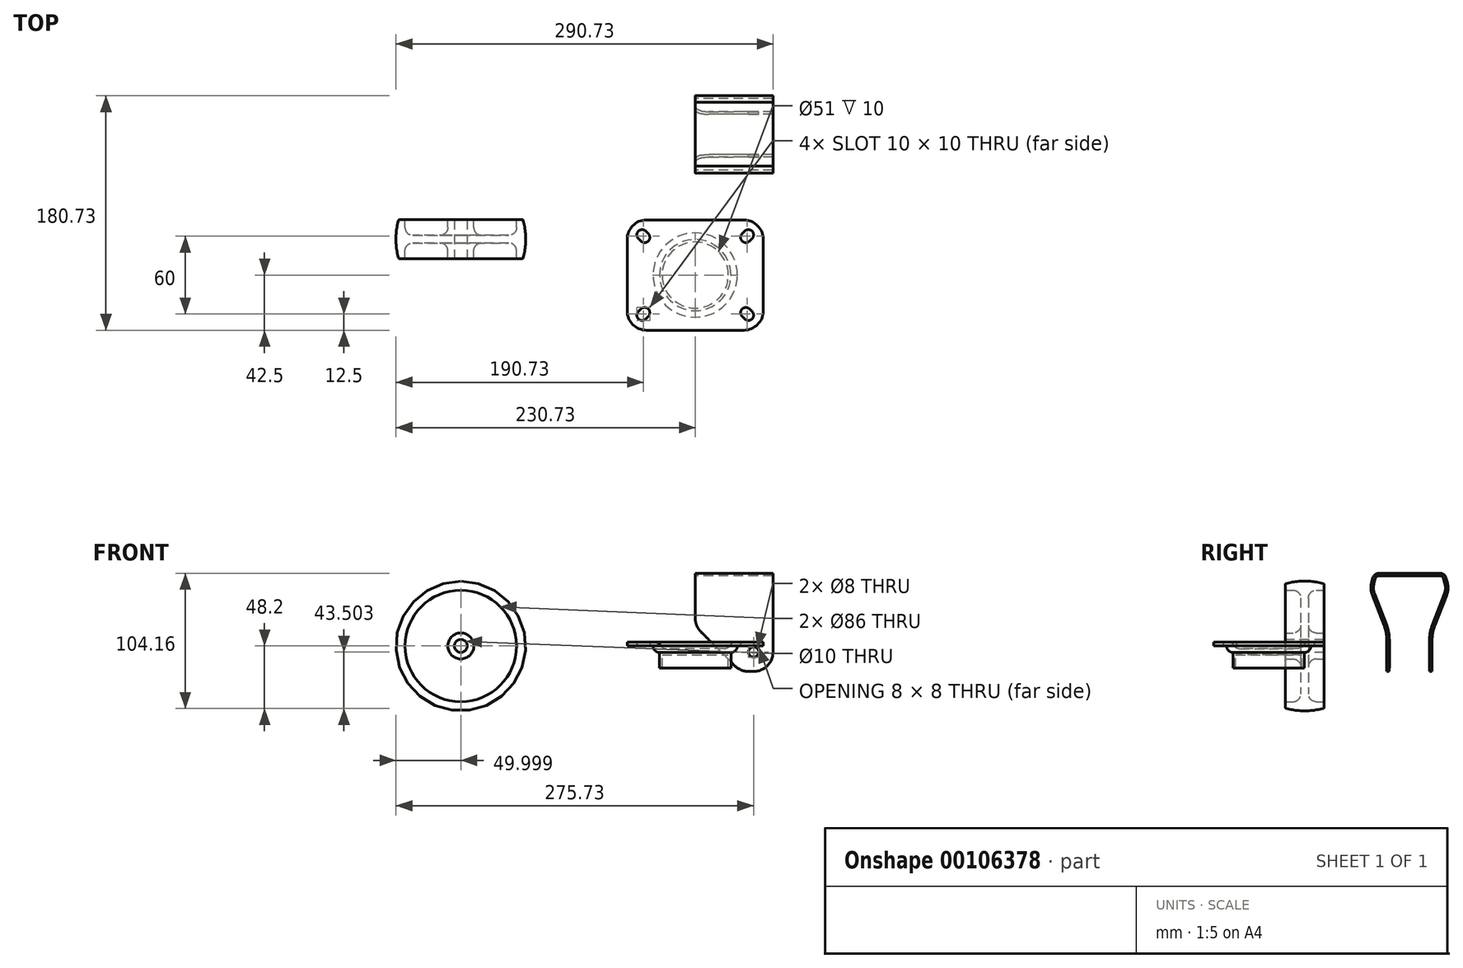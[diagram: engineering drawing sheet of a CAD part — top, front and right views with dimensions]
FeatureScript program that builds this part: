
annotation { "Feature Type Name" : "Feature", "Feature Type Description" : "" }
export const myFeature = defineFeature(function(context is Context, id is Id, definition is map)
    precondition{}
    {
        {
            var Q0;
            Q0=qCreatedBy(makeId("Top.planeOp"),FACE);
            var sketch = newSketch(context, id + "F0", { "sketchPlane" : qUnion([Q0])});
            skLineSegment(sketch, "E0.bottom", {"start": v(37.5, -42.5) * mm, "end": v(-37.5, -42.5) * mm});
            skLineSegment(sketch, "E0.top", {"start": v(37.5, 42.5) * mm, "end": v(-37.5, 42.5) * mm});
            skLineSegment(sketch, "E0.left", {"start": v(52.5, -27.5) * mm, "end": v(52.5, 27.5) * mm});
            skLineSegment(sketch, "E0.right", {"start": v(-52.5, -27.5) * mm, "end": v(-52.5, 27.5) * mm});
            skPoint(sketch, "E0.middle", {"position": v(0, 0) * mm});
            skLineSegment(sketch, "E1.bottom", {"start": v(41, -31) * mm, "end": v(-41, -31) * mm, "construction": true});
            skLineSegment(sketch, "E1.top", {"start": v(41, 31) * mm, "end": v(-41, 31) * mm, "construction": true});
            skLineSegment(sketch, "E1.left", {"start": v(41, -31) * mm, "end": v(41, 31) * mm, "construction": true});
            skLineSegment(sketch, "E1.right", {"start": v(-41, -31) * mm, "end": v(-41, 31) * mm, "construction": true});
            skLineSegment(sketch, "E2.bottom", {"start": v(39, -29) * mm, "end": v(-39, -29) * mm, "construction": true});
            skLineSegment(sketch, "E2.top", {"start": v(39, 29) * mm, "end": v(-39, 29) * mm, "construction": true});
            skLineSegment(sketch, "E2.left", {"start": v(39, -29) * mm, "end": v(39, 29) * mm, "construction": true});
            skLineSegment(sketch, "E2.right", {"start": v(-39, -29) * mm, "end": v(-39, 29) * mm, "construction": true});
            skArc(sketch, "E3", {"start": v(-38.17, 33.83) * mm, "mid": v(-43.83, 33.83) * mm, "end": v(-43.83, 28.17) * mm});
            skArc(sketch, "E4", {"start": v(-41.83, 26.17) * mm, "mid": v(-36.17, 26.17) * mm, "end": v(-36.17, 31.83) * mm});
            skLineSegment(sketch, "E5", {"start": v(-38.17, 33.83) * mm, "end": v(-36.17, 31.83) * mm});
            skLineSegment(sketch, "E6", {"start": v(-43.83, 28.17) * mm, "end": v(-41.83, 26.17) * mm});
            skLineSegment(sketch, "E7", {"start": v(0, 42.5) * mm, "end": v(0, -42.5) * mm, "construction": true});
            skLineSegment(sketch, "E8", {"start": v(-52.5, 0) * mm, "end": v(52.5, 0) * mm, "construction": true});
            skLineSegment(sketch, "E9.MirrorCS", {"start": v(43.83, 28.17) * mm, "end": v(41.83, 26.17) * mm});
            skLineSegment(sketch, "E10.MirrorCS", {"start": v(38.17, 33.83) * mm, "end": v(36.17, 31.83) * mm});
            skArc(sketch, "E11.MirrorCS", {"start": v(38.17, 33.83) * mm, "mid": v(43.83, 33.83) * mm, "end": v(43.83, 28.17) * mm});
            skArc(sketch, "E12.MirrorCS", {"start": v(41.83, 26.17) * mm, "mid": v(36.17, 26.17) * mm, "end": v(36.17, 31.83) * mm});
            skLineSegment(sketch, "E13.MirrorCS", {"start": v(52.5, 0) * mm, "end": v(-52.5, 0) * mm, "construction": true});
            skLineSegment(sketch, "E14.MirrorCS", {"start": v(43.83, -28.17) * mm, "end": v(41.83, -26.17) * mm});
            skLineSegment(sketch, "E15.MirrorCS", {"start": v(38.17, -33.83) * mm, "end": v(36.17, -31.83) * mm});
            skLineSegment(sketch, "E16.MirrorCS", {"start": v(-38.17, -33.83) * mm, "end": v(-36.17, -31.83) * mm});
            skLineSegment(sketch, "E17.MirrorCS", {"start": v(-43.83, -28.17) * mm, "end": v(-41.83, -26.17) * mm});
            skArc(sketch, "E18.MirrorCS", {"start": v(38.17, -33.83) * mm, "mid": v(43.83, -33.83) * mm, "end": v(43.83, -28.17) * mm});
            skArc(sketch, "E19.MirrorCS", {"start": v(41.83, -26.17) * mm, "mid": v(36.17, -26.17) * mm, "end": v(36.17, -31.83) * mm});
            skArc(sketch, "E20.MirrorCS", {"start": v(-38.17, -33.83) * mm, "mid": v(-43.83, -33.83) * mm, "end": v(-43.83, -28.17) * mm});
            skArc(sketch, "E21.MirrorCS", {"start": v(-41.83, -26.17) * mm, "mid": v(-36.17, -26.17) * mm, "end": v(-36.17, -31.83) * mm});
            skPoint(sketch, "E22.visualSharp", {"position": v(-52.5, 42.5) * mm});
            skArc(sketch, "E22.filletArc", {"start": v(-37.5, 42.5) * mm, "mid": v(-48.1, 38.1) * mm, "end": v(-52.5, 27.5) * mm});
            skPoint(sketch, "E23.visualSharp", {"position": v(-52.5, -42.5) * mm});
            skArc(sketch, "E23.filletArc", {"start": v(-52.5, -27.5) * mm, "mid": v(-48.1, -38.1) * mm, "end": v(-37.5, -42.5) * mm});
            skPoint(sketch, "E24.visualSharp", {"position": v(52.5, -42.5) * mm});
            skArc(sketch, "E24.filletArc", {"start": v(37.5, -42.5) * mm, "mid": v(48.1, -38.1) * mm, "end": v(52.5, -27.5) * mm});
            skPoint(sketch, "E25.visualSharp", {"position": v(52.5, 42.5) * mm});
            skArc(sketch, "E25.filletArc", {"start": v(52.5, 27.5) * mm, "mid": v(48.1, 38.1) * mm, "end": v(37.5, 42.5) * mm});
            skSolve(sketch);
        }
        {
            var Q0;
            Q0 = qSketchRegion(id + "F0", true);
            extrude(context, id + "F1", {"entities" : qUnion([Q0]), "depth" : 3 * mm});
        }
        {
            var Q0;
            Q0=makeQuery(id+"F1.opExtrude","CAP_FACE",FACE,{"disambiguationData":[OSD([sQuery(id+"F0.wireOp",EDGE,"E0.bottom"),sQuery(id+"F0.wireOp",EDGE,"E0.top"),sQuery(id+"F0.wireOp",EDGE,"E0.left"),sQuery(id+"F0.wireOp",EDGE,"E0.right"),sQuery(id+"F0.wireOp",EDGE,"E3"),sQuery(id+"F0.wireOp",EDGE,"E4"),sQuery(id+"F0.wireOp",EDGE,"E5"),sQuery(id+"F0.wireOp",EDGE,"E6"),sQuery(id+"F0.wireOp",EDGE,"E9.MirrorCS"),sQuery(id+"F0.wireOp",EDGE,"E10.MirrorCS"),sQuery(id+"F0.wireOp",EDGE,"E11.MirrorCS"),sQuery(id+"F0.wireOp",EDGE,"E12.MirrorCS"),sQuery(id+"F0.wireOp",EDGE,"E14.MirrorCS"),sQuery(id+"F0.wireOp",EDGE,"E15.MirrorCS"),sQuery(id+"F0.wireOp",EDGE,"E16.MirrorCS"),sQuery(id+"F0.wireOp",EDGE,"E17.MirrorCS"),sQuery(id+"F0.wireOp",EDGE,"E18.MirrorCS"),sQuery(id+"F0.wireOp",EDGE,"E20.MirrorCS"),sQuery(id+"F0.wireOp",EDGE,"E21.MirrorCS"),sQuery(id+"F0.wireOp",EDGE,"E19.MirrorCS"),sQuery(id+"F0.wireOp",EDGE,"E22.filletArc"),sQuery(id+"F0.wireOp",EDGE,"E23.filletArc"),sQuery(id+"F0.wireOp",EDGE,"E24.filletArc"),sQuery(id+"F0.wireOp",EDGE,"E25.filletArc")])],"isStart":true});
            var sketch = newSketch(context, id + "F2", { "sketchPlane" : qUnion([Q0])});
            skCircle(sketch, "E26", {"center": v(0, 0) * mm, "radius": 32.5 * mm});
            skSolve(sketch);
        }
        {
            var Q0;
            Q0 = qSketchRegion(id + "F2", true);
            extrude(context, id + "F3", {"entities" : qUnion([Q0]), "operationType" : NewBodyOperationType.ADD, "depth" : 5 * mm});
        }
        {
            var Q0;
            Q0=makeQuery(id+"F3.opExtrude","CAP_EDGE",EDGE,{"disambiguationData":[OSD([sQuery(id+"F2.wireOp",EDGE,"E26")])],"isStart":false});
            fillet(context, id + "F4", {"entities" : qUnion([Q0]), "radius" : 5 * mm, "tangentPropagation" : true, "allowEdgeOverflow" : false});
        }
        {
            var Q0;
            Q0=makeQuery(id+"F1.opExtrude","CAP_FACE",FACE,{"disambiguationData":[OSD([sQuery(id+"F0.wireOp",EDGE,"E0.bottom"),sQuery(id+"F0.wireOp",EDGE,"E0.top"),sQuery(id+"F0.wireOp",EDGE,"E0.left"),sQuery(id+"F0.wireOp",EDGE,"E0.right"),sQuery(id+"F0.wireOp",EDGE,"E3"),sQuery(id+"F0.wireOp",EDGE,"E4"),sQuery(id+"F0.wireOp",EDGE,"E5"),sQuery(id+"F0.wireOp",EDGE,"E6"),sQuery(id+"F0.wireOp",EDGE,"E9.MirrorCS"),sQuery(id+"F0.wireOp",EDGE,"E10.MirrorCS"),sQuery(id+"F0.wireOp",EDGE,"E11.MirrorCS"),sQuery(id+"F0.wireOp",EDGE,"E12.MirrorCS"),sQuery(id+"F0.wireOp",EDGE,"E14.MirrorCS"),sQuery(id+"F0.wireOp",EDGE,"E15.MirrorCS"),sQuery(id+"F0.wireOp",EDGE,"E16.MirrorCS"),sQuery(id+"F0.wireOp",EDGE,"E17.MirrorCS"),sQuery(id+"F0.wireOp",EDGE,"E18.MirrorCS"),sQuery(id+"F0.wireOp",EDGE,"E20.MirrorCS"),sQuery(id+"F0.wireOp",EDGE,"E21.MirrorCS"),sQuery(id+"F0.wireOp",EDGE,"E19.MirrorCS"),sQuery(id+"F0.wireOp",EDGE,"E22.filletArc"),sQuery(id+"F0.wireOp",EDGE,"E23.filletArc"),sQuery(id+"F0.wireOp",EDGE,"E24.filletArc"),sQuery(id+"F0.wireOp",EDGE,"E25.filletArc")])],"isStart":false});
            var sketch = newSketch(context, id + "F5", { "sketchPlane" : qUnion([Q0])});
            skCircle(sketch, "E27", {"center": v(0, 0) * mm, "radius": 27.5 * mm});
            skSolve(sketch);
        }
        {
            var Q0;
            Q0 = qSketchRegion(id + "F5", true);
            extrude(context, id + "F6", {"entities" : qUnion([Q0]), "operationType" : NewBodyOperationType.REMOVE, "oppositeDirection" : true, "depth" : 5 * mm});
        }
        {
            var Q0;
            Q0=makeQuery(id+"F6.boolean.opBoolean","COPY",EDGE,{"derivedFrom":makeQuery(id+"F6.opExtrude","CAP_EDGE",EDGE,{"disambiguationData":[OSD([sQuery(id+"F5.wireOp",EDGE,"E27")])],"isStart":false})});
            fillet(context, id + "F7", {"entities" : qUnion([Q0]), "radius" : 5 * mm, "tangentPropagation" : true, "allowEdgeOverflow" : false});
        }
        {
            var Q0;
            Q0=makeQuery(id+"F7.opFillet","BLEND_EDGE",EDGE,{"blendedFrom":[makeQuery(id+"F6.boolean.opBoolean","COPY",EDGE,{"derivedFrom":makeQuery(id+"F6.opExtrude","CAP_EDGE",EDGE,{"disambiguationData":[OSD([sQuery(id+"F5.wireOp",EDGE,"E27")])],"isStart":false})}),makeQuery(id+"F1.opExtrude","CAP_FACE",FACE,{"disambiguationData":[OSD([sQuery(id+"F0.wireOp",EDGE,"E0.bottom"),sQuery(id+"F0.wireOp",EDGE,"E0.top"),sQuery(id+"F0.wireOp",EDGE,"E0.left"),sQuery(id+"F0.wireOp",EDGE,"E0.right"),sQuery(id+"F0.wireOp",EDGE,"E3"),sQuery(id+"F0.wireOp",EDGE,"E4"),sQuery(id+"F0.wireOp",EDGE,"E5"),sQuery(id+"F0.wireOp",EDGE,"E6"),sQuery(id+"F0.wireOp",EDGE,"E9.MirrorCS"),sQuery(id+"F0.wireOp",EDGE,"E10.MirrorCS"),sQuery(id+"F0.wireOp",EDGE,"E11.MirrorCS"),sQuery(id+"F0.wireOp",EDGE,"E12.MirrorCS"),sQuery(id+"F0.wireOp",EDGE,"E14.MirrorCS"),sQuery(id+"F0.wireOp",EDGE,"E15.MirrorCS"),sQuery(id+"F0.wireOp",EDGE,"E16.MirrorCS"),sQuery(id+"F0.wireOp",EDGE,"E17.MirrorCS"),sQuery(id+"F0.wireOp",EDGE,"E18.MirrorCS"),sQuery(id+"F0.wireOp",EDGE,"E20.MirrorCS"),sQuery(id+"F0.wireOp",EDGE,"E21.MirrorCS"),sQuery(id+"F0.wireOp",EDGE,"E19.MirrorCS"),sQuery(id+"F0.wireOp",EDGE,"E22.filletArc"),sQuery(id+"F0.wireOp",EDGE,"E23.filletArc"),sQuery(id+"F0.wireOp",EDGE,"E24.filletArc"),sQuery(id+"F0.wireOp",EDGE,"E25.filletArc")])],"isStart":false})],"blendedInto":[makeQuery(id+"F1.opExtrude","CAP_FACE",FACE,{"disambiguationData":[OSD([sQuery(id+"F0.wireOp",EDGE,"E0.bottom"),sQuery(id+"F0.wireOp",EDGE,"E0.top"),sQuery(id+"F0.wireOp",EDGE,"E0.left"),sQuery(id+"F0.wireOp",EDGE,"E0.right"),sQuery(id+"F0.wireOp",EDGE,"E3"),sQuery(id+"F0.wireOp",EDGE,"E4"),sQuery(id+"F0.wireOp",EDGE,"E5"),sQuery(id+"F0.wireOp",EDGE,"E6"),sQuery(id+"F0.wireOp",EDGE,"E9.MirrorCS"),sQuery(id+"F0.wireOp",EDGE,"E10.MirrorCS"),sQuery(id+"F0.wireOp",EDGE,"E11.MirrorCS"),sQuery(id+"F0.wireOp",EDGE,"E12.MirrorCS"),sQuery(id+"F0.wireOp",EDGE,"E14.MirrorCS"),sQuery(id+"F0.wireOp",EDGE,"E15.MirrorCS"),sQuery(id+"F0.wireOp",EDGE,"E16.MirrorCS"),sQuery(id+"F0.wireOp",EDGE,"E17.MirrorCS"),sQuery(id+"F0.wireOp",EDGE,"E18.MirrorCS"),sQuery(id+"F0.wireOp",EDGE,"E20.MirrorCS"),sQuery(id+"F0.wireOp",EDGE,"E21.MirrorCS"),sQuery(id+"F0.wireOp",EDGE,"E19.MirrorCS"),sQuery(id+"F0.wireOp",EDGE,"E22.filletArc"),sQuery(id+"F0.wireOp",EDGE,"E23.filletArc"),sQuery(id+"F0.wireOp",EDGE,"E24.filletArc"),sQuery(id+"F0.wireOp",EDGE,"E25.filletArc")])],"isStart":false})]});
            fillet(context, id + "F8", {"entities" : qUnion([Q0]), "radius" : 5 * mm, "tangentPropagation" : true, "allowEdgeOverflow" : false});
        }
        {
            var Q0;
            Q0=makeQuery(id+"F3.opExtrude","CAP_FACE",FACE,{"disambiguationData":[OSD([sQuery(id+"F2.wireOp",EDGE,"E26")])],"isStart":false});
            var sketch = newSketch(context, id + "F9", { "sketchPlane" : qUnion([Q0])});
            skCircle(sketch, "E28", {"center": v(0, 0) * mm, "radius": 27.5 * mm});
            skSolve(sketch);
        }
        {
            var Q0;
            Q0 = qSketchRegion(id + "F9", true);
            extrude(context, id + "F10", {"entities" : qUnion([Q0]), "depth" : 2 * mm});
        }
        {
            var Q0;
            Q0=makeQuery(id+"F10.opExtrude","CAP_FACE",FACE,{"disambiguationData":[OSD([sQuery(id+"F9.wireOp",EDGE,"E28")])],"isStart":false});
            var sketch = newSketch(context, id + "F11", { "sketchPlane" : qUnion([Q0])});
            skCircle(sketch, "E29", {"center": v(0, 0) * mm, "radius": 27.5 * mm});
            skCircle(sketch, "E30.0", {"center": v(0, 0) * mm, "radius": 25.5 * mm});
            skSolve(sketch);
        }
        {
            var Q0;
            Q0 = qSketchRegion(id + "F11", true);
            extrude(context, id + "F12", {"entities" : qUnion([Q0]), "operationType" : NewBodyOperationType.ADD, "depth" : 10 * mm});
        }
        {
            var Q0;
            Q0=qCreatedBy(makeId("Top.planeOp"),FACE);
            var sketch = newSketch(context, id + "F13", { "sketchPlane" : qUnion([Q0])});
            skLineSegment(sketch, "E31.bottom", {"start": v(-230.73, 12.69) * mm, "end": v(-130.73, 12.69) * mm, "construction": true});
            skLineSegment(sketch, "E31.top", {"start": v(-230.73, 42.69) * mm, "end": v(-130.73, 42.69) * mm, "construction": true});
            skLineSegment(sketch, "E31.right", {"start": v(-130.73, 12.69) * mm, "end": v(-130.73, 42.69) * mm, "construction": true});
            skLineSegment(sketch, "E32", {"start": v(-130.73, 27.69) * mm, "end": v(-230.73, 27.69) * mm, "construction": true});
            skLineSegment(sketch, "E33", {"start": v(-230.73, 42.69) * mm, "end": v(-230.73, 12.69) * mm, "construction": true});
            skLineSegment(sketch, "E34", {"start": v(-180.73, 42.69) * mm, "end": v(-180.73, 12.69) * mm, "construction": true});
            skLineSegment(sketch, "E35", {"start": v(-180.73, 27.69) * mm, "end": v(-180.73, 42.69) * mm});
            skLineSegment(sketch, "E36", {"start": v(-190.73, 41.69) * mm, "end": v(-190.73, 36.69) * mm});
            skLineSegment(sketch, "E37", {"start": v(-196.73, 30.69) * mm, "end": v(-217.73, 30.69) * mm});
            skLineSegment(sketch, "E38", {"start": v(-223.73, 36.69) * mm, "end": v(-223.73, 41.69) * mm});
            skLineSegment(sketch, "E39", {"start": v(-224.73, 42.69) * mm, "end": v(-227.96, 42.69) * mm});
            skPoint(sketch, "E40.visualSharp", {"position": v(-223.73, 30.69) * mm});
            skArc(sketch, "E40.filletArc", {"start": v(-223.73, 36.69) * mm, "mid": v(-221.97, 32.45) * mm, "end": v(-217.73, 30.69) * mm});
            skPoint(sketch, "E41.visualSharp", {"position": v(-190.73, 30.69) * mm});
            skArc(sketch, "E41.filletArc", {"start": v(-196.73, 30.69) * mm, "mid": v(-192.49, 32.45) * mm, "end": v(-190.73, 36.69) * mm});
            skArc(sketch, "E42", {"start": v(-228.93, 41.94) * mm, "mid": v(-230.73, 27.69) * mm, "end": v(-228.93, 13.44) * mm});
            skLineSegment(sketch, "E43", {"start": v(-189.73, 42.69) * mm, "end": v(-180.73, 42.69) * mm});
            skArc(sketch, "E44.MirrorCS", {"start": v(-223.73, 18.69) * mm, "mid": v(-221.97, 22.93) * mm, "end": v(-217.73, 24.69) * mm});
            skLineSegment(sketch, "E45.MirrorCS", {"start": v(-196.73, 24.69) * mm, "end": v(-217.73, 24.69) * mm});
            skLineSegment(sketch, "E46.MirrorCS", {"start": v(-223.73, 18.69) * mm, "end": v(-223.73, 13.69) * mm});
            skLineSegment(sketch, "E47.MirrorCS", {"start": v(-224.73, 12.69) * mm, "end": v(-227.96, 12.69) * mm});
            skArc(sketch, "E48.MirrorCS", {"start": v(-196.73, 24.69) * mm, "mid": v(-192.49, 22.93) * mm, "end": v(-190.73, 18.69) * mm});
            skLineSegment(sketch, "E49.MirrorCS", {"start": v(-190.73, 13.69) * mm, "end": v(-190.73, 18.69) * mm});
            skLineSegment(sketch, "E50.MirrorCS", {"start": v(-189.73, 12.69) * mm, "end": v(-180.73, 12.69) * mm});
            skLineSegment(sketch, "E51.MirrorCS", {"start": v(-180.73, 27.69) * mm, "end": v(-180.73, 12.69) * mm});
            skPoint(sketch, "E52.visualSharp", {"position": v(-228.73, 42.69) * mm});
            skArc(sketch, "E52.filletArc", {"start": v(-227.96, 42.69) * mm, "mid": v(-228.57, 42.48) * mm, "end": v(-228.93, 41.94) * mm});
            skPoint(sketch, "E53.visualSharp", {"position": v(-223.73, 42.69) * mm});
            skArc(sketch, "E53.filletArc", {"start": v(-223.73, 41.69) * mm, "mid": v(-224.02, 42.4) * mm, "end": v(-224.73, 42.69) * mm});
            skPoint(sketch, "E54.visualSharp", {"position": v(-190.73, 42.69) * mm});
            skArc(sketch, "E54.filletArc", {"start": v(-189.73, 42.69) * mm, "mid": v(-190.44, 42.4) * mm, "end": v(-190.73, 41.69) * mm});
            skPoint(sketch, "E55.visualSharp", {"position": v(-228.73, 12.69) * mm});
            skArc(sketch, "E55.filletArc", {"start": v(-228.93, 13.44) * mm, "mid": v(-228.57, 12.9) * mm, "end": v(-227.96, 12.69) * mm});
            skPoint(sketch, "E56.visualSharp", {"position": v(-223.73, 12.69) * mm});
            skArc(sketch, "E56.filletArc", {"start": v(-224.73, 12.69) * mm, "mid": v(-224.02, 12.98) * mm, "end": v(-223.73, 13.69) * mm});
            skPoint(sketch, "E57.visualSharp", {"position": v(-190.73, 12.69) * mm});
            skArc(sketch, "E57.filletArc", {"start": v(-190.73, 13.69) * mm, "mid": v(-190.44, 12.98) * mm, "end": v(-189.73, 12.69) * mm});
            skSolve(sketch);
        }
        {
            var Q0;
            Q0=sQuery(id+"F13.wireOp",VERTEX,"E51.MirrorCS.start");
            var Q1;
            Q1=qCreatedBy(makeId("Front.planeOp"),FACE);
            cPlane(context, id + "F14", {"entities" : qUnion([Q0, Q1]), "cplaneType" : CPlaneType.PLANE_POINT, "offset" : 25 * mm, "width" : 150 * mm, "height" : 150 * mm});
        }
        {
            var Q0;
            Q0=makeQuery(id+"F13.imprint","IMPRINT",FACE,{"disambiguationData":[TD([[makeQuery(id+"F13.imprint","IMPRINT",EDGE,{"derivedFrom":sQuery(id+"F13.wireOp",EDGE,"E35")}),1.0]])]});
            var Q1;
            Q1=sQuery(id+"F13.wireOp",EDGE,"E51.MirrorCS");
            revolve(context, id + "F15", {"entities" : qUnion([Q0]), "axis" : qUnion([Q1]), "revolveType" : RevolveType.FULL});
        }
        {
            var Q0;
            Q0=makeQuery(id+"F15.opRevolve","SWEPT_FACE",FACE,{"disambiguationData":[OSD([sQuery(id+"F13.wireOp",EDGE,"E50.MirrorCS")])]});
            var sketch = newSketch(context, id + "F16", { "sketchPlane" : qUnion([Q0])});
            skCircle(sketch, "E58", {"center": v(-180.73, 0) * mm, "radius": 5 * mm});
            skSolve(sketch);
        }
        {
            var Q0;
            Q0 = qSketchRegion(id + "F16", true);
            extrude(context, id + "F17", {"entities" : qUnion([Q0]), "operationType" : NewBodyOperationType.REMOVE, "endBound" : BoundingType.THROUGH_ALL, "oppositeDirection" : true, "depth" : 25 * mm});
        }
        {
            var Q0;
            Q0=qCreatedBy(makeId("Right.planeOp"),FACE);
            var sketch = newSketch(context, id + "F18", { "sketchPlane" : qUnion([Q0])});
            skLineSegment(sketch, "E59.bottom", {"start": v(135.97, -19.7) * mm, "end": v(80.97, -19.7) * mm, "construction": true});
            skLineSegment(sketch, "E59.left", {"start": v(135.97, -19.7) * mm, "end": v(136, 55.3) * mm, "construction": true});
            skLineSegment(sketch, "E59.right", {"start": v(80.97, -19.7) * mm, "end": v(81, 55.3) * mm, "construction": true});
            skPoint(sketch, "E59.middle", {"position": v(108.49, 17.8) * mm});
            skLineSegment(sketch, "E60", {"start": v(136.76, 52.33) * mm, "end": v(137.76, 48.45) * mm});
            skLineSegment(sketch, "E61", {"start": v(137.22, 39.3) * mm, "end": v(128, 15.53) * mm});
            skLineSegment(sketch, "E62", {"start": v(125.97, 4.7) * mm, "end": v(125.97, -19.7) * mm});
            skLineSegment(sketch, "E63", {"start": v(108.5, 55.3) * mm, "end": v(108.47, -19.7) * mm, "construction": true});
            skPoint(sketch, "E64.visualSharp", {"position": v(136, 55.3) * mm});
            skArc(sketch, "E64.filletArc", {"start": v(136.76, 52.33) * mm, "mid": v(135.44, 54.64) * mm, "end": v(133.12, 55.94) * mm});
            skPoint(sketch, "E65.visualSharp", {"position": v(138.95, 43.79) * mm});
            skArc(sketch, "E65.filletArc", {"start": v(137.22, 39.3) * mm, "mid": v(138.2, 43.83) * mm, "end": v(137.76, 48.45) * mm});
            skPoint(sketch, "E66.visualSharp", {"position": v(125.97, 10.3) * mm});
            skArc(sketch, "E66.filletArc", {"start": v(128, 15.53) * mm, "mid": v(126.49, 10.2) * mm, "end": v(125.97, 4.7) * mm});
            skLineSegment(sketch, "E67.MirrorCS", {"start": v(80.97, -19.68) * mm, "end": v(81, 55.32) * mm, "construction": true});
            skLineSegment(sketch, "E68", {"start": v(83.89, 55.96) * mm, "end": v(133.12, 55.94) * mm});
            skLineSegment(sketch, "E69.0", {"start": v(123.97, 4.7) * mm, "end": v(123.97, -19.7) * mm});
            skArc(sketch, "E69.1", {"start": v(126.14, 16.26) * mm, "mid": v(124.52, 10.57) * mm, "end": v(123.97, 4.7) * mm});
            skLineSegment(sketch, "E69.2", {"start": v(135.35, 40.02) * mm, "end": v(126.14, 16.26) * mm});
            skLineSegment(sketch, "E69.9", {"start": v(84.16, 53.96) * mm, "end": v(132.84, 53.94) * mm});
            skArc(sketch, "E69.10", {"start": v(134.83, 51.83) * mm, "mid": v(134.1, 53.14) * mm, "end": v(132.84, 53.94) * mm});
            skLineSegment(sketch, "E69.11", {"start": v(134.83, 51.83) * mm, "end": v(135.82, 47.95) * mm});
            skArc(sketch, "E69.12", {"start": v(135.35, 40.02) * mm, "mid": v(136.2, 43.95) * mm, "end": v(135.82, 47.95) * mm});
            skLineSegment(sketch, "E70", {"start": v(123.97, -19.7) * mm, "end": v(125.97, -19.7) * mm});
            skLineSegment(sketch, "E71.MirrorCS", {"start": v(92.97, -19.69) * mm, "end": v(90.97, -19.69) * mm});
            skLineSegment(sketch, "E72.MirrorCS", {"start": v(93, 4.7) * mm, "end": v(92.97, -19.69) * mm});
            skLineSegment(sketch, "E73.MirrorCS", {"start": v(91, 4.7) * mm, "end": v(90.97, -19.69) * mm});
            skLineSegment(sketch, "E74.MirrorCS", {"start": v(82.17, 51.85) * mm, "end": v(81.17, 47.97) * mm});
            skArc(sketch, "E75.MirrorCS", {"start": v(82.17, 51.85) * mm, "mid": v(82.9, 53.16) * mm, "end": v(84.16, 53.96) * mm});
            skLineSegment(sketch, "E76.MirrorCS", {"start": v(80.24, 52.35) * mm, "end": v(79.24, 48.47) * mm});
            skArc(sketch, "E77.MirrorCS", {"start": v(80.24, 52.35) * mm, "mid": v(81.56, 54.66) * mm, "end": v(83.89, 55.96) * mm});
            skArc(sketch, "E78.MirrorCS", {"start": v(79.77, 39.32) * mm, "mid": v(78.8, 43.85) * mm, "end": v(79.24, 48.47) * mm});
            skArc(sketch, "E79.MirrorCS", {"start": v(88.97, 15.55) * mm, "mid": v(90.48, 10.22) * mm, "end": v(91, 4.7) * mm});
            skLineSegment(sketch, "E80.MirrorCS", {"start": v(79.77, 39.32) * mm, "end": v(88.97, 15.55) * mm});
            skLineSegment(sketch, "E81.MirrorCS", {"start": v(81.64, 40.04) * mm, "end": v(90.84, 16.27) * mm});
            skArc(sketch, "E82.MirrorCS", {"start": v(90.84, 16.27) * mm, "mid": v(92.45, 10.59) * mm, "end": v(93, 4.7) * mm});
            skPoint(sketch, "E83.MirrorP", {"position": v(91, 10.31) * mm});
            skArc(sketch, "E84.MirrorCS", {"start": v(81.64, 40.04) * mm, "mid": v(80.79, 43.97) * mm, "end": v(81.17, 47.97) * mm});
            skPoint(sketch, "E85.MirrorP", {"position": v(81, 55.32) * mm});
            skPoint(sketch, "E86.MirrorP", {"position": v(78.04, 43.81) * mm});
            skSolve(sketch);
        }
        {
            var Q0;
            Q0 = qSketchRegion(id + "F18", true);
            extrude(context, id + "F19", {"entities" : qUnion([Q0]), "depth" : 60 * mm});
        }
        {
            var Q0;
            Q0=makeQuery(id+"F19.opExtrude","SWEPT_FACE",FACE,{"disambiguationData":[OSD([sQuery(id+"F18.wireOp",EDGE,"E62")])]});
            var sketch = newSketch(context, id + "F20", { "sketchPlane" : qUnion([Q0])});
            skLineSegment(sketch, "E87.bottom", {"start": v(-60, -19.7) * mm, "end": v(-45, -19.7) * mm, "construction": true});
            skLineSegment(sketch, "E87.top", {"start": v(-60, -4.7) * mm, "end": v(-45, -4.7) * mm, "construction": true});
            skLineSegment(sketch, "E87.left", {"start": v(-60, -19.7) * mm, "end": v(-60, -4.7) * mm, "construction": true});
            skLineSegment(sketch, "E87.right", {"start": v(-45, -19.7) * mm, "end": v(-45, -4.7) * mm, "construction": true});
            skCircle(sketch, "E88", {"center": v(-45, -4.7) * mm, "radius": 4 * mm});
            skSolve(sketch);
        }
        {
            var Q0;
            Q0=makeQuery(id+"F19.opExtrude","CAP_EDGE",EDGE,{"disambiguationData":[OSD([sQuery(id+"F18.wireOp",EDGE,"E70")])],"isStart":true});
            var Q1;
            Q1=makeQuery(id+"F19.opExtrude","CAP_EDGE",EDGE,{"disambiguationData":[OSD([sQuery(id+"F18.wireOp",EDGE,"E71.MirrorCS")])],"isStart":true});
            chamfer(context, id + "F21", {"entities" : qUnion([Q0, Q1]), "width" : 35 * mm, "tangentPropagation" : true});
        }
        {
            var Q0;
            {var subQ0=sQuery(id+"F18.wireOp",EDGE,"E70");Q0=makeQuery(id+"F21.opChamfer","BLEND_EDGE",EDGE,{"blendedFrom":[makeQuery(id+"F19.opExtrude","CAP_EDGE",EDGE,{"disambiguationData":[OSD([subQ0])],"isStart":true}),makeQuery(id+"F19.opExtrude","SWEPT_FACE",FACE,{"disambiguationData":[OSD([subQ0])]})],"blendedInto":[makeQuery(id+"F19.opExtrude","SWEPT_FACE",FACE,{"disambiguationData":[OSD([subQ0])]})]});}
            var Q1;
            {var subQ0=sQuery(id+"F18.wireOp",EDGE,"E71.MirrorCS");Q1=makeQuery(id+"F21.opChamfer","BLEND_EDGE",EDGE,{"blendedFrom":[makeQuery(id+"F19.opExtrude","CAP_EDGE",EDGE,{"disambiguationData":[OSD([subQ0])],"isStart":true}),makeQuery(id+"F19.opExtrude","SWEPT_FACE",FACE,{"disambiguationData":[OSD([subQ0])]})],"blendedInto":[makeQuery(id+"F19.opExtrude","SWEPT_FACE",FACE,{"disambiguationData":[OSD([subQ0])]})]});}
            var Q2;
            {var subQ0=sQuery(id+"F18.wireOp",EDGE,"E70");Q2=makeQuery(id+"F21.opChamfer","BLEND_EDGE",EDGE,{"blendedFrom":[makeQuery(id+"F19.opExtrude","CAP_EDGE",EDGE,{"disambiguationData":[OSD([subQ0])],"isStart":true}),makeQuery(id+"F19.opExtrude","CAP_FACE",FACE,{"disambiguationData":[OSD([sQuery(id+"F18.wireOp",EDGE,"E60"),sQuery(id+"F18.wireOp",EDGE,"E61"),sQuery(id+"F18.wireOp",EDGE,"E62"),sQuery(id+"F18.wireOp",EDGE,"E64.filletArc"),sQuery(id+"F18.wireOp",EDGE,"E65.filletArc"),sQuery(id+"F18.wireOp",EDGE,"E66.filletArc"),sQuery(id+"F18.wireOp",EDGE,"E68"),sQuery(id+"F18.wireOp",EDGE,"E69.0"),sQuery(id+"F18.wireOp",EDGE,"E69.1"),sQuery(id+"F18.wireOp",EDGE,"E69.2"),sQuery(id+"F18.wireOp",EDGE,"E69.9"),sQuery(id+"F18.wireOp",EDGE,"E69.10"),sQuery(id+"F18.wireOp",EDGE,"E69.11"),sQuery(id+"F18.wireOp",EDGE,"E69.12"),subQ0,sQuery(id+"F18.wireOp",EDGE,"E71.MirrorCS"),sQuery(id+"F18.wireOp",EDGE,"E72.MirrorCS"),sQuery(id+"F18.wireOp",EDGE,"E73.MirrorCS"),sQuery(id+"F18.wireOp",EDGE,"E74.MirrorCS"),sQuery(id+"F18.wireOp",EDGE,"E75.MirrorCS"),sQuery(id+"F18.wireOp",EDGE,"E76.MirrorCS"),sQuery(id+"F18.wireOp",EDGE,"E77.MirrorCS"),sQuery(id+"F18.wireOp",EDGE,"E78.MirrorCS"),sQuery(id+"F18.wireOp",EDGE,"E79.MirrorCS"),sQuery(id+"F18.wireOp",EDGE,"E80.MirrorCS"),sQuery(id+"F18.wireOp",EDGE,"E81.MirrorCS"),sQuery(id+"F18.wireOp",EDGE,"E82.MirrorCS"),sQuery(id+"F18.wireOp",EDGE,"E84.MirrorCS")])],"isStart":true})],"blendedInto":[makeQuery(id+"F19.opExtrude","CAP_FACE",FACE,{"disambiguationData":[OSD([sQuery(id+"F18.wireOp",EDGE,"E60"),sQuery(id+"F18.wireOp",EDGE,"E61"),sQuery(id+"F18.wireOp",EDGE,"E62"),sQuery(id+"F18.wireOp",EDGE,"E64.filletArc"),sQuery(id+"F18.wireOp",EDGE,"E65.filletArc"),sQuery(id+"F18.wireOp",EDGE,"E66.filletArc"),sQuery(id+"F18.wireOp",EDGE,"E68"),sQuery(id+"F18.wireOp",EDGE,"E69.0"),sQuery(id+"F18.wireOp",EDGE,"E69.1"),sQuery(id+"F18.wireOp",EDGE,"E69.2"),sQuery(id+"F18.wireOp",EDGE,"E69.9"),sQuery(id+"F18.wireOp",EDGE,"E69.10"),sQuery(id+"F18.wireOp",EDGE,"E69.11"),sQuery(id+"F18.wireOp",EDGE,"E69.12"),subQ0,sQuery(id+"F18.wireOp",EDGE,"E71.MirrorCS"),sQuery(id+"F18.wireOp",EDGE,"E72.MirrorCS"),sQuery(id+"F18.wireOp",EDGE,"E73.MirrorCS"),sQuery(id+"F18.wireOp",EDGE,"E74.MirrorCS"),sQuery(id+"F18.wireOp",EDGE,"E75.MirrorCS"),sQuery(id+"F18.wireOp",EDGE,"E76.MirrorCS"),sQuery(id+"F18.wireOp",EDGE,"E77.MirrorCS"),sQuery(id+"F18.wireOp",EDGE,"E78.MirrorCS"),sQuery(id+"F18.wireOp",EDGE,"E79.MirrorCS"),sQuery(id+"F18.wireOp",EDGE,"E80.MirrorCS"),sQuery(id+"F18.wireOp",EDGE,"E81.MirrorCS"),sQuery(id+"F18.wireOp",EDGE,"E82.MirrorCS"),sQuery(id+"F18.wireOp",EDGE,"E84.MirrorCS")])],"isStart":true})]});}
            var Q3;
            {var subQ0=sQuery(id+"F18.wireOp",EDGE,"E71.MirrorCS");Q3=makeQuery(id+"F21.opChamfer","BLEND_EDGE",EDGE,{"blendedFrom":[makeQuery(id+"F19.opExtrude","CAP_EDGE",EDGE,{"disambiguationData":[OSD([subQ0])],"isStart":true}),makeQuery(id+"F19.opExtrude","CAP_FACE",FACE,{"disambiguationData":[OSD([sQuery(id+"F18.wireOp",EDGE,"E60"),sQuery(id+"F18.wireOp",EDGE,"E61"),sQuery(id+"F18.wireOp",EDGE,"E62"),sQuery(id+"F18.wireOp",EDGE,"E64.filletArc"),sQuery(id+"F18.wireOp",EDGE,"E65.filletArc"),sQuery(id+"F18.wireOp",EDGE,"E66.filletArc"),sQuery(id+"F18.wireOp",EDGE,"E68"),sQuery(id+"F18.wireOp",EDGE,"E69.0"),sQuery(id+"F18.wireOp",EDGE,"E69.1"),sQuery(id+"F18.wireOp",EDGE,"E69.2"),sQuery(id+"F18.wireOp",EDGE,"E69.9"),sQuery(id+"F18.wireOp",EDGE,"E69.10"),sQuery(id+"F18.wireOp",EDGE,"E69.11"),sQuery(id+"F18.wireOp",EDGE,"E69.12"),sQuery(id+"F18.wireOp",EDGE,"E70"),subQ0,sQuery(id+"F18.wireOp",EDGE,"E72.MirrorCS"),sQuery(id+"F18.wireOp",EDGE,"E73.MirrorCS"),sQuery(id+"F18.wireOp",EDGE,"E74.MirrorCS"),sQuery(id+"F18.wireOp",EDGE,"E75.MirrorCS"),sQuery(id+"F18.wireOp",EDGE,"E76.MirrorCS"),sQuery(id+"F18.wireOp",EDGE,"E77.MirrorCS"),sQuery(id+"F18.wireOp",EDGE,"E78.MirrorCS"),sQuery(id+"F18.wireOp",EDGE,"E79.MirrorCS"),sQuery(id+"F18.wireOp",EDGE,"E80.MirrorCS"),sQuery(id+"F18.wireOp",EDGE,"E81.MirrorCS"),sQuery(id+"F18.wireOp",EDGE,"E82.MirrorCS"),sQuery(id+"F18.wireOp",EDGE,"E84.MirrorCS")])],"isStart":true})],"blendedInto":[makeQuery(id+"F19.opExtrude","CAP_FACE",FACE,{"disambiguationData":[OSD([sQuery(id+"F18.wireOp",EDGE,"E60"),sQuery(id+"F18.wireOp",EDGE,"E61"),sQuery(id+"F18.wireOp",EDGE,"E62"),sQuery(id+"F18.wireOp",EDGE,"E64.filletArc"),sQuery(id+"F18.wireOp",EDGE,"E65.filletArc"),sQuery(id+"F18.wireOp",EDGE,"E66.filletArc"),sQuery(id+"F18.wireOp",EDGE,"E68"),sQuery(id+"F18.wireOp",EDGE,"E69.0"),sQuery(id+"F18.wireOp",EDGE,"E69.1"),sQuery(id+"F18.wireOp",EDGE,"E69.2"),sQuery(id+"F18.wireOp",EDGE,"E69.9"),sQuery(id+"F18.wireOp",EDGE,"E69.10"),sQuery(id+"F18.wireOp",EDGE,"E69.11"),sQuery(id+"F18.wireOp",EDGE,"E69.12"),sQuery(id+"F18.wireOp",EDGE,"E70"),subQ0,sQuery(id+"F18.wireOp",EDGE,"E72.MirrorCS"),sQuery(id+"F18.wireOp",EDGE,"E73.MirrorCS"),sQuery(id+"F18.wireOp",EDGE,"E74.MirrorCS"),sQuery(id+"F18.wireOp",EDGE,"E75.MirrorCS"),sQuery(id+"F18.wireOp",EDGE,"E76.MirrorCS"),sQuery(id+"F18.wireOp",EDGE,"E77.MirrorCS"),sQuery(id+"F18.wireOp",EDGE,"E78.MirrorCS"),sQuery(id+"F18.wireOp",EDGE,"E79.MirrorCS"),sQuery(id+"F18.wireOp",EDGE,"E80.MirrorCS"),sQuery(id+"F18.wireOp",EDGE,"E81.MirrorCS"),sQuery(id+"F18.wireOp",EDGE,"E82.MirrorCS"),sQuery(id+"F18.wireOp",EDGE,"E84.MirrorCS")])],"isStart":true})]});}
            var Q4;
            Q4=makeQuery(id+"F19.opExtrude","CAP_EDGE",EDGE,{"disambiguationData":[OSD([sQuery(id+"F18.wireOp",EDGE,"E70")])],"isStart":false});
            var Q5;
            Q5=makeQuery(id+"F19.opExtrude","CAP_EDGE",EDGE,{"disambiguationData":[OSD([sQuery(id+"F18.wireOp",EDGE,"E71.MirrorCS")])],"isStart":false});
            fillet(context, id + "F22", {"entities" : qUnion([Q0, Q1, Q2, Q3, Q4, Q5]), "radius" : 15 * mm, "tangentPropagation" : true, "allowEdgeOverflow" : false});
        }
        {
            var Q0;
            Q0 = qSketchRegion(id + "F20", true);
            extrude(context, id + "F23", {"entities" : qUnion([Q0]), "operationType" : NewBodyOperationType.REMOVE, "endBound" : BoundingType.THROUGH_ALL, "oppositeDirection" : true, "depth" : 25 * mm});
        }
    });
